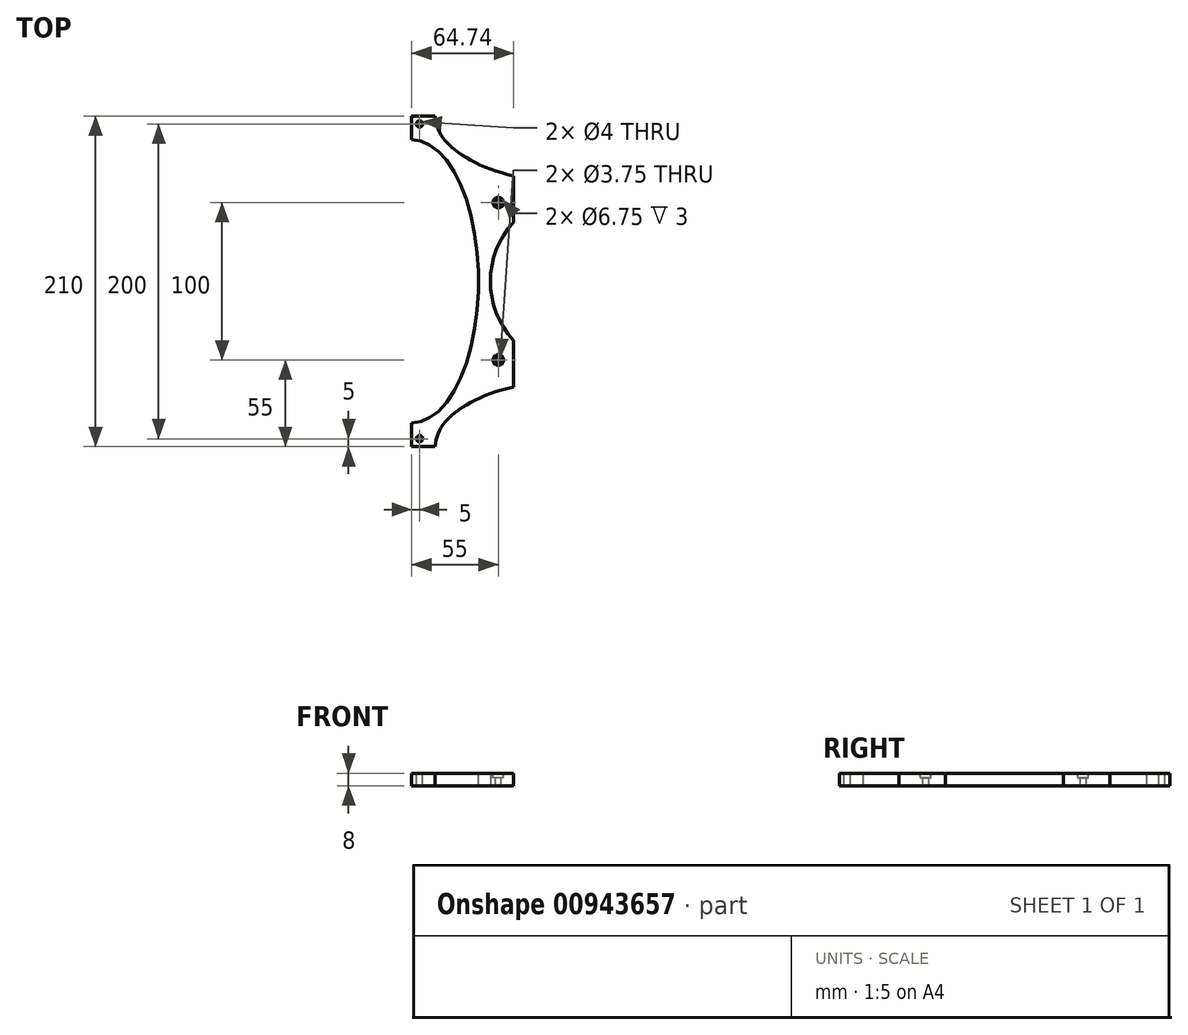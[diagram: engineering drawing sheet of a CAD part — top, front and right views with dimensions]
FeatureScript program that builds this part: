
annotation { "Feature Type Name" : "Feature", "Feature Type Description" : "" }
export const myFeature = defineFeature(function(context is Context, id is Id, definition is map)
    precondition{}
    {
        {
            var Q0;
            Q0=qCreatedBy(makeId("Top.planeOp"),FACE);
            var sketch = newSketch(context, id + "F0", { "sketchPlane" : qUnion([Q0])});
            skLineSegment(sketch, "E0.bottom", {"start": v(105, 105) * mm, "end": v(-105, 105) * mm});
            skLineSegment(sketch, "E0.top", {"start": v(105, -105) * mm, "end": v(-105, -105) * mm});
            skLineSegment(sketch, "E0.left", {"start": v(105, 105) * mm, "end": v(105, -105) * mm});
            skLineSegment(sketch, "E0.right", {"start": v(-105, 105) * mm, "end": v(-105, -105) * mm});
            skPoint(sketch, "E0.middle", {"position": v(0, 0) * mm});
            skCircle(sketch, "E1", {"center": v(0, 0) * mm, "radius": 55 * mm});
            skEllipse(sketch, "E2", {"center": v(-105, 0) * mm, "majorRadius": 90 * mm, "minorRadius": 42.5 * mm, "majorAxis": v(0, 1)});
            skEllipse(sketch, "E3", {"center": v(0, 105) * mm, "majorRadius": 90 * mm, "minorRadius": 42.5 * mm, "majorAxis": v(1, 0)});
            skEllipse(sketch, "E4", {"center": v(105, 0) * mm, "majorRadius": 90 * mm, "minorRadius": 42.5 * mm, "majorAxis": v(0, 1)});
            skEllipse(sketch, "E5", {"center": v(0, -105) * mm, "majorRadius": 90 * mm, "minorRadius": 42.5 * mm, "majorAxis": v(1, 0)});
            skSolve(sketch);
        }
        {
            var Q0;
            Q0=makeQuery(id+"F0.imprint","IMPRINT",FACE,{"disambiguationData":[TD([[makeQuery(id+"F0.imprint","IMPRINT",EDGE,{"derivedFrom":sQuery(id+"F0.wireOp",EDGE,"E1")}),-1.0]])]});
            extrude(context, id + "F1", {"entities" : qUnion([Q0]), "depth" : 8 * mm, "offsetDistance" : 25 * mm});
        }
        {
            var Q0;
            Q0=makeQuery(id+"F1.opExtrude","CAP_FACE",FACE,{"disambiguationData":[OSD([sQuery(id+"F0.wireOp",EDGE,"E0.bottom"),sQuery(id+"F0.wireOp",EDGE,"E0.top"),sQuery(id+"F0.wireOp",EDGE,"E0.left"),sQuery(id+"F0.wireOp",EDGE,"E0.right")])],"isStart":false});
            var sketch = newSketch(context, id + "F2", { "sketchPlane" : qUnion([Q0])});
            skPoint(sketch, "E6", {"position": v(-50, 50) * mm});
            skPoint(sketch, "E7", {"position": v(50, 50) * mm});
            skPoint(sketch, "E8", {"position": v(50, -50) * mm});
            skPoint(sketch, "E9", {"position": v(-50, -50) * mm});
            skPoint(sketch, "E10", {"position": v(-100, 100) * mm});
            skPoint(sketch, "E11", {"position": v(100, 100) * mm});
            skPoint(sketch, "E12", {"position": v(100, -100) * mm});
            skPoint(sketch, "E13", {"position": v(-100, -100) * mm});
            skSolve(sketch);
        }
        {
            var Q0;
            Q0=sQuery(id+"F2.wireOp",VERTEX,"E10");
            var Q1;
            Q1=sQuery(id+"F2.wireOp",VERTEX,"E11");
            var Q2;
            Q2=sQuery(id+"F2.wireOp",VERTEX,"E12");
            var Q3;
            Q3=sQuery(id+"F2.wireOp",VERTEX,"E13");
            var Q4;
            Q4=makeQuery(id+"F1.opExtrude","SWEPT_BODY",BODY,{"disambiguationData":[OSD([sQuery(id+"F0.wireOp",EDGE,"E0.bottom"),sQuery(id+"F0.wireOp",EDGE,"E0.top"),sQuery(id+"F0.wireOp",EDGE,"E0.left"),sQuery(id+"F0.wireOp",EDGE,"E0.right")])]});
            hole(context, id + "F3", {"style" : HoleStyle.SIMPLE, "endStyle" : HoleEndStyle.THROUGH, "holeDiameter" : 4 * mm, "majorDiameter" : 5 * mm, "isTappedThrough" : true, "tappedDepth" : 12 * mm, "tapClearance" : 3, "locations" : qUnion([Q0, Q1, Q2, Q3]), "scope" : qUnion([Q4])});
        }
        {
            var Q0;
            Q0=sQuery(id+"F2.wireOp",VERTEX,"E6");
            var Q1;
            Q1=sQuery(id+"F2.wireOp",VERTEX,"E9");
            var Q2;
            Q2=sQuery(id+"F2.wireOp",VERTEX,"E8");
            var Q3;
            Q3=sQuery(id+"F2.wireOp",VERTEX,"E7");
            var Q4;
            Q4=makeQuery(id+"F1.opExtrude","SWEPT_BODY",BODY,{"disambiguationData":[OSD([sQuery(id+"F0.wireOp",EDGE,"E0.bottom"),sQuery(id+"F0.wireOp",EDGE,"E0.top"),sQuery(id+"F0.wireOp",EDGE,"E0.left"),sQuery(id+"F0.wireOp",EDGE,"E0.right")])]});
            hole(context, id + "F4", {"style" : HoleStyle.C_BORE, "endStyle" : HoleEndStyle.THROUGH, "holeDiameter" : 3.75 * mm, "cBoreDiameter" : 6.75 * mm, "cBoreDepth" : 3 * mm, "majorDiameter" : 5 * mm, "isTappedThrough" : true, "tappedDepth" : 12 * mm, "tapClearance" : 3, "locations" : qUnion([Q0, Q1, Q2, Q3]), "scope" : qUnion([Q4])});
        }
        {
            var Q0;
            Q0=qCreatedBy(makeId("Top.planeOp"),FACE);
            var sketch = newSketch(context, id + "F5", { "sketchPlane" : qUnion([Q0])});
            skLineSegment(sketch, "E14.bottom", {"start": v(40.26, 122.7) * mm, "end": v(-40.26, 122.7) * mm});
            skLineSegment(sketch, "E14.top", {"start": v(40.26, -122.7) * mm, "end": v(-40.26, -122.7) * mm});
            skLineSegment(sketch, "E14.left", {"start": v(40.26, 122.7) * mm, "end": v(40.26, -122.7) * mm});
            skLineSegment(sketch, "E14.right", {"start": v(-40.26, 122.7) * mm, "end": v(-40.26, -122.7) * mm});
            skPoint(sketch, "E14.middle", {"position": v(0, 0) * mm});
            skLineSegment(sketch, "E15.bottom", {"start": v(40.26, 122.7) * mm, "end": v(115.16, 122.7) * mm});
            skLineSegment(sketch, "E15.top", {"start": v(40.26, -122.7) * mm, "end": v(115.16, -122.7) * mm});
            skLineSegment(sketch, "E15.right", {"start": v(115.16, 122.7) * mm, "end": v(115.16, -122.7) * mm});
            skSolve(sketch);
        }
        {
            var Q0;
            Q0 = qSketchRegion(id + "F5", true);
            extrude(context, id + "F6", {"entities" : qUnion([Q0]), "operationType" : NewBodyOperationType.REMOVE, "depth" : 25 * mm, "offsetDistance" : 25 * mm});
        }
    });
